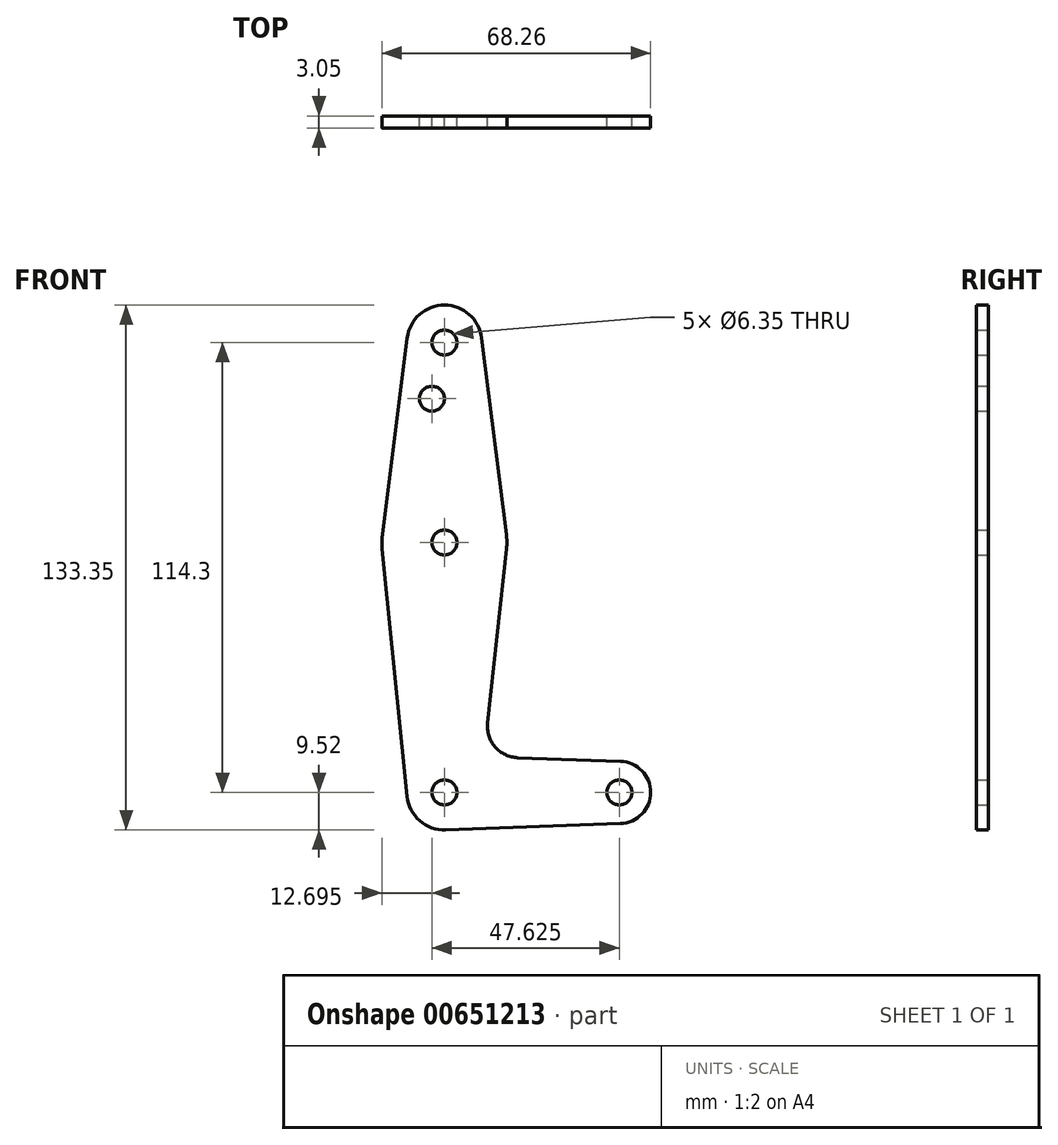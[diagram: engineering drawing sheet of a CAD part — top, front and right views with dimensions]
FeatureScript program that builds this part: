
annotation { "Feature Type Name" : "Feature", "Feature Type Description" : "" }
export const myFeature = defineFeature(function(context is Context, id is Id, definition is map)
    precondition{}
    {
        {
            var Q0;
            Q0=qCreatedBy(makeId("Front.planeOp"),FACE);
            var sketch = newSketch(context, id + "F0", { "sketchPlane" : qUnion([Q0])});
            skLineSegment(sketch, "E0", {"start": v(0, 0) * mm, "end": v(0, 63.5) * mm, "construction": true});
            skLineSegment(sketch, "E1", {"start": v(0, 63.5) * mm, "end": v(0, 114.3) * mm, "construction": true});
            skLineSegment(sketch, "E2", {"start": v(0, 0) * mm, "end": v(44.45, 0) * mm, "construction": true});
            skCircle(sketch, "E3", {"center": v(0, 114.3) * mm, "radius": 9.53 * mm});
            skCircle(sketch, "E4", {"center": v(0, 63.5) * mm, "radius": 15.88 * mm});
            skCircle(sketch, "E5", {"center": v(0, 0) * mm, "radius": 9.53 * mm});
            skCircle(sketch, "E6", {"center": v(44.45, 0) * mm, "radius": 7.94 * mm});
            skLineSegment(sketch, "E7", {"start": v(-9.45, 115.5) * mm, "end": v(-15.75, 65.48) * mm});
            skLineSegment(sketch, "E8", {"start": v(9.45, 115.5) * mm, "end": v(15.75, 65.48) * mm});
            skLineSegment(sketch, "E9", {"start": v(44.72, 7.93) * mm, "end": v(18.63, 8.82) * mm});
            skLineSegment(sketch, "E10", {"start": v(44.73, -7.93) * mm, "end": v(0, -9.53) * mm});
            skLineSegment(sketch, "E11", {"start": v(-9.48, -0.95) * mm, "end": v(-15.8, 61.91) * mm});
            skLineSegment(sketch, "E12", {"start": v(11, 17.63) * mm, "end": v(15.78, 61.79) * mm});
            skArc(sketch, "E13.filletArc", {"start": v(11, 17.63) * mm, "mid": v(12.9, 11.56) * mm, "end": v(18.63, 8.82) * mm});
            skCircle(sketch, "E14", {"center": v(0, 114.3) * mm, "radius": 3.18 * mm});
            skCircle(sketch, "E15", {"center": v(0, 63.5) * mm, "radius": 3.18 * mm});
            skCircle(sketch, "E16", {"center": v(0, 0) * mm, "radius": 3.18 * mm});
            skCircle(sketch, "E17", {"center": v(44.45, 0) * mm, "radius": 3.18 * mm});
            skCircle(sketch, "E18", {"center": v(-3.18, 100.03) * mm, "radius": 3.18 * mm});
            skSolve(sketch);
        }
        {
            var Q0;
            Q0 = qSketchRegion(id + "F0", true);
            extrude(context, id + "F1", {"entities" : qUnion([Q0]), "depth" : 3.05 * mm, "offsetDistance" : 25.4 * mm});
        }
    });
